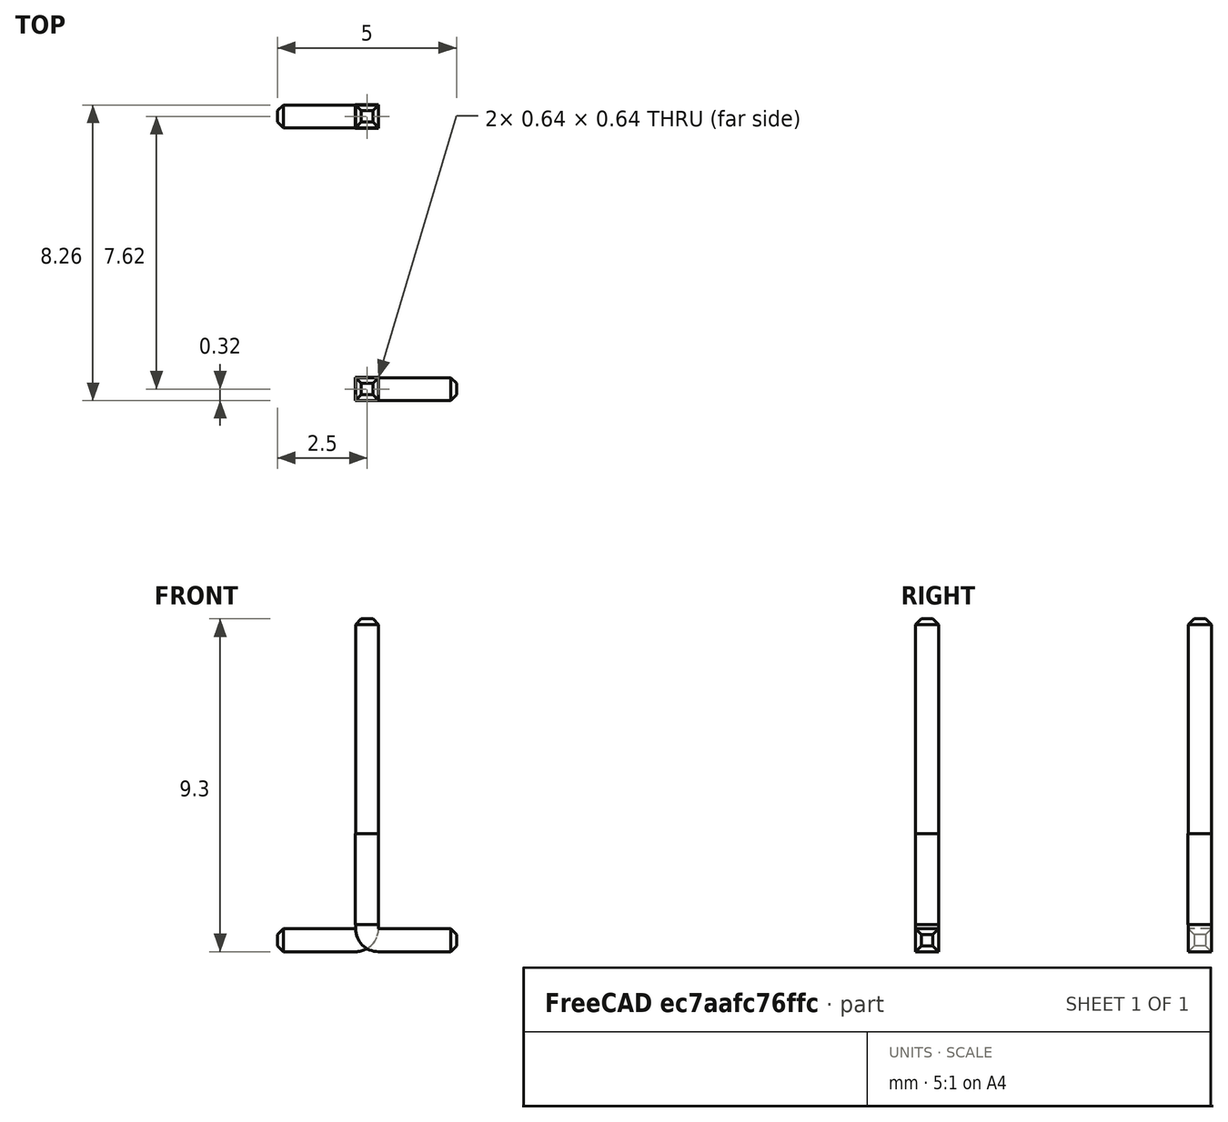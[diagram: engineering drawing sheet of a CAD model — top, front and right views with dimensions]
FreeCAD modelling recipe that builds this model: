
FCSTD DOCUMENT  (FreeCAD 0.16R6712 (Git))
Label: Neo-reverse-4-Pin
License: All rights reserved
LicenseURL: http://en.wikipedia.org/wiki/All_rights_reserved
objects: Part::Box×5, Part::Cut×5, Part::Feature×1, Part::FeaturePython×1
note: 12 computed .brp shape members not serialized (recipe doc carries the construction recipe); baked Part::Feature solids carry a one-line shape summary decoded from their .brp

FEATURE [Part::Feature] Part__Feature  label="PinHeader_1x04_P254mm_Vertical_SMD_Pin1Left"
  shape: bbox 5 x 10.16 x 9.3 mm, 112 faces (baked)
FEATURE [Part::Box] Box  label="Cube"
  Height = 12
  Length = 8
  Placement = pos=(-4,-3.48,-1) rot=(0,0,1;0rad)
  Width = 6.96
FEATURE [Part::Cut] Cut
  Base = -> Part__Feature
  Tool = -> Box
FEATURE [Part::FeaturePython] Clone  label="Clone of Cut"  # Draft clone (typed FeaturePython)
  Objects = -> [Cut]
  Scale = (1,1,1)
FEATURE [Part::Box] Box001  label="Cube001"
  Height = 10
  Length = 1.2
  Placement = pos=(0.321,-6,0.65) rot=(0,0,1;0rad)
  Width = 12
FEATURE [Part::Box] Box002  label="Cube002"
  Height = 10
  Length = 1.2
  Placement = pos=(-1.529,-6,0.65) rot=(0,0,1;0rad)
  Width = 12
FEATURE [Part::Box] Box003  label="Cube003"
  Height = 10
  Length = 3
  Placement = pos=(-1.529,-6,0.65) rot=(0,0,1;0rad)
  Width = 1.868
FEATURE [Part::Box] Box004  label="Cube004"
  Height = 10
  Length = 3
  Placement = pos=(-1.529,4.134,0.4) rot=(0,0,1;0rad)
  Width = 1.868
FEATURE [Part::Cut] Cut001
  Base = -> Clone
  Tool = -> Box001
FEATURE [Part::Cut] Cut002
  Base = -> Cut001
  Tool = -> Box002
FEATURE [Part::Cut] Cut003
  Base = -> Cut002
  Tool = -> Box003
FEATURE [Part::Cut] Cut004
  Base = -> Cut003
  Tool = -> Box004
